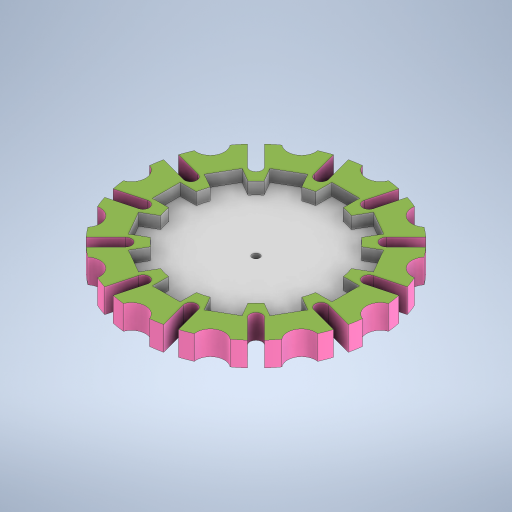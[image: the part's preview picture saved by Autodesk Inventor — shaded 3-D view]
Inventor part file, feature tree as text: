
AUTODESK INVENTOR PART (.ipt)
format: ipt  version: 2023 (Build 270158000, 158)  size: 565,248 bytes
history: native  units: mm
features: sketch x4, extrude x2
ambient origin geometry x8: Origin, YZ Plane, XZ Plane, XY Plane, X Axis, Y Axis, Z Axis, Center Point
bodies: Solid1 (feature_tree)
feature tree (6):
  sketch  "Sketch1"  dims[d1=80.0mm d2=100.0mm d3=22.5deg d4=20.712mm d5=50.0mm d6=54.123064mm d7=10.0mm d8=25.858174mm d9=65.0mm d10=360.0deg d11=7.0mm d12=7.0mm d13=15.0mm d14=15.0mm d15=10.0mm d16=200.0mm]
  extrude  "Extrusion1"  Depth=10.0mm
  sketch  "Sketch3"  dims[d20=10.0mm]
  extrude  "Extrusion3"  TaperAngle=90.0deg  [1 undecoded]
  sketch  "Sketch2"  dims[d17=15.0deg d19=90.0deg]
  sketch  "Sketch4"  dims[d21=10.0mm d22=80.0mm d23=120.0mm d25=360.0deg d27=6.0mm d28=5.0mm d29=20.0mm d30=0.0mm d34=120.0mm d36=360.0deg d41=120.0mm d42=124.403mm d43=23.006mm d44=14.13mm d46=14.13mm d48=360.0deg d49=10.0mm d50=0.0mm]
note: 1 required parameter value undecoded (feature->parameter linkage not recoverable at this tier; creation-order binding heuristic only, values carry confidence <= 0.55)
